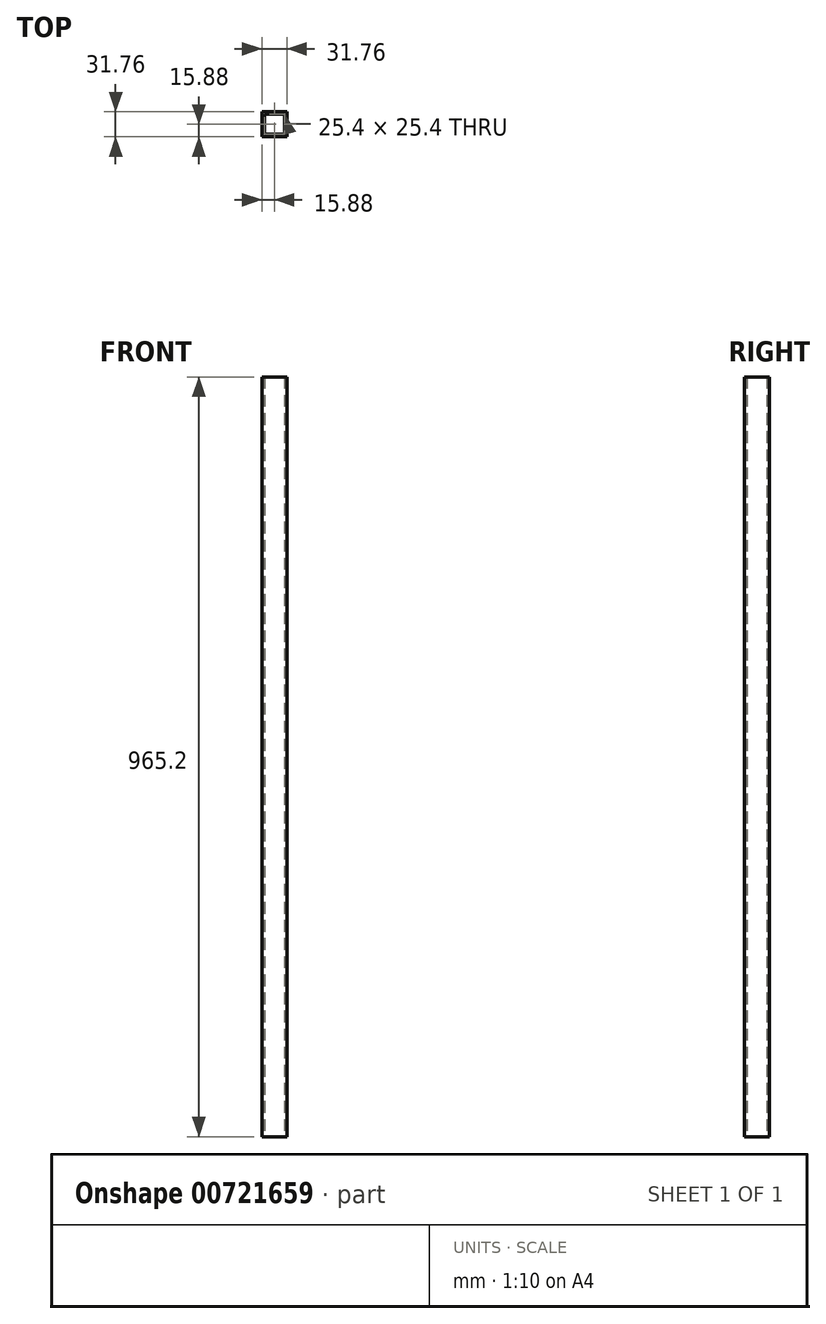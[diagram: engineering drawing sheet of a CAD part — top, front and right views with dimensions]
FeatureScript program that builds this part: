
annotation { "Feature Type Name" : "Feature", "Feature Type Description" : "" }
export const myFeature = defineFeature(function(context is Context, id is Id, definition is map)
    precondition{}
    {
        {
            var Q0;
            Q0=qCreatedBy(makeId("Top.planeOp"),FACE);
            var sketch = newSketch(context, id + "F0", { "sketchPlane" : qUnion([Q0])});
            skLineSegment(sketch, "E0.bottom", {"start": v(12.7, 12.7) * mm, "end": v(-12.7, 12.7) * mm});
            skLineSegment(sketch, "E0.top", {"start": v(12.7, -12.7) * mm, "end": v(-12.7, -12.7) * mm});
            skLineSegment(sketch, "E0.left", {"start": v(12.7, 12.7) * mm, "end": v(12.7, -12.7) * mm});
            skLineSegment(sketch, "E0.right", {"start": v(-12.7, 12.7) * mm, "end": v(-12.7, -12.7) * mm});
            skPoint(sketch, "E0.middle", {"position": v(0, 0) * mm});
            skLineSegment(sketch, "E1.0", {"start": v(15.88, -15.88) * mm, "end": v(-15.88, -15.88) * mm});
            skLineSegment(sketch, "E1.1", {"start": v(15.88, 15.88) * mm, "end": v(15.88, -15.88) * mm});
            skLineSegment(sketch, "E1.2", {"start": v(15.88, 15.88) * mm, "end": v(-15.88, 15.88) * mm});
            skLineSegment(sketch, "E1.3", {"start": v(-15.88, 15.88) * mm, "end": v(-15.88, -15.88) * mm});
            skSolve(sketch);
        }
        {
            var Q0;
            Q0 = qSketchRegion(id + "F0", true);
            extrude(context, id + "F1", {"entities" : qUnion([Q0]), "depth" : 965.2 * mm, "offsetDistance" : 25.4 * mm});
        }
        {
            var Q0;
            Q0=makeQuery(id+"F1.opExtrude","CAP_FACE",FACE,{"disambiguationData":[OSD([sQuery(id+"F0.wireOp",EDGE,"E0.bottom"),sQuery(id+"F0.wireOp",EDGE,"E0.top"),sQuery(id+"F0.wireOp",EDGE,"E0.left"),sQuery(id+"F0.wireOp",EDGE,"E0.right"),sQuery(id+"F0.wireOp",EDGE,"E1.0"),sQuery(id+"F0.wireOp",EDGE,"E1.1"),sQuery(id+"F0.wireOp",EDGE,"E1.2"),sQuery(id+"F0.wireOp",EDGE,"E1.3")])],"isStart":false});
            var sketch = newSketch(context, id + "F2", { "sketchPlane" : qUnion([Q0])});
            skLineSegment(sketch, "E2", {"start": v(-15.88, 15.88) * mm, "end": v(15.88, -15.88) * mm, "construction": true});
            skSolve(sketch);
        }
    });
